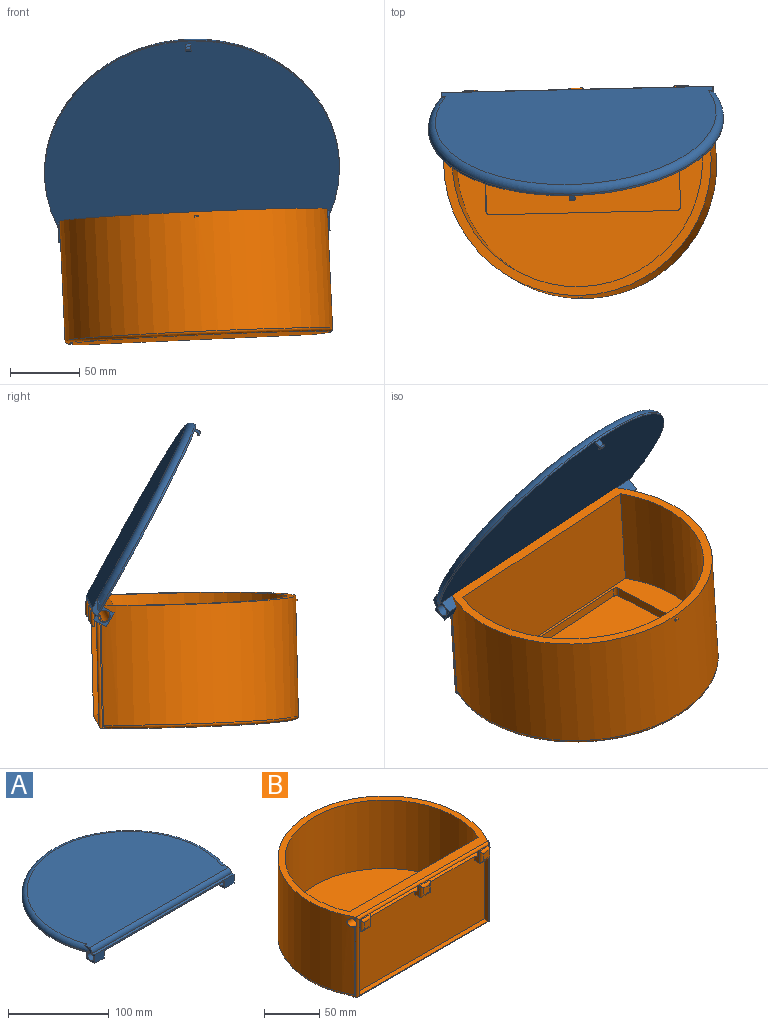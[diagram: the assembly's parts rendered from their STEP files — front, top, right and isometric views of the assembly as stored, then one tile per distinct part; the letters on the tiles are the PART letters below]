
ASSEMBLY  parts=2 mates=1
PART A: 29 faces, bbox 230.7x165x15.4 mm
  f0: plane 169.48x3.67mm, normal (0,0,-1), area 621.6mm2, adj f19,f20,f24,f27
  f1: plane 213.09x148.55mm, normal (0,0,-1), area 26333.1mm2, adj f2,f3,f4,f5,f11,f12,f15,f19
  f2: plane 15.37x14.01mm, normal (-1,0,0), area 79.2mm2, adj f1,f3,f6,f7,f8,f10,f21,f23
  f3: cylinder r=106.54mm len=213.09mm, axis (0,0,-1), area 534.7mm2, adj f1,f2,f5,f7,f27,f28
  f4: plane 5.72x3.64mm, normal (1,0,0), area 12.3mm2, adj f1,f12,f13,f14,f15,f16,f17,f18
  f5: plane 15.37x14.01mm, normal (1,0,0), area 79.2mm2, adj f1,f3,f6,f7,f8,f9,f21,f22
  f6: cylinder r=5.08mm len=195.82mm, axis (1,0,0), area 1318.5mm2, adj f2,f5,f8,f21
  f7: torus R=101.46mm, axis (0,0,1), area 3251.5mm2, adj f2,f3,f5,f8,f9,f10
  f8: plane 202.93x143.47mm, normal (0,0,1), area 24499mm2, adj f2,f5,f6,f7,f9,f10
  f9: plane 2.98x0.86mm, normal (0,1,0), area 0.8mm2, adj f5,f7,f8
  f10: plane 2.98x0.86mm, normal (0,1,0), area 0.8mm2, adj f2,f7,f8
  f11: plane 5.72x3.64mm, normal (-1,0,0), area 12.3mm2, adj f1,f12,f13,f14,f15,f16,f17,f18
  f12: plane 4.45x3.81mm, normal (0,1,0), area 16.9mm2, adj f1,f4,f11,f18
  f13: plane 3.81x1.27mm, normal (0,0,-1), area 4.8mm2, adj f4,f11,f16,f18
  f14: plane 3.81x0.64mm, normal (0,0,1), area 2.4mm2, adj f4,f11,f15,f17
  f15: plane 4.45x3.81mm, normal (0,-1,0), area 16.9mm2, adj f1,f4,f11,f14
  f16: cylinder r=1.27mm len=3.81mm, axis (1,0,0), area 5.1mm2, adj f4,f11,f13,f17
  f17: cylinder r=1.27mm len=3.81mm, axis (-1,0,0), area 5.1mm2, adj f4,f11,f14,f16
  f18: cylinder r=1.27mm len=3.81mm, axis (-1,0,0), area 7.6mm2, adj f4,f11,f12,f13
  f19: plane 11.47x9.02mm, normal (-1,0,0), area 43.3mm2, adj f0,f1,f22,f24,f25,f27
  f20: plane 11.47x9.02mm, normal (1,0,0), area 43.3mm2, adj f0,f1,f23,f24,f26,f27
  f21: plane 195.82x3.81mm, normal (0,0,1), area 746.1mm2, adj f2,f5,f6,f24
  f22: plane 13.17x9.02mm, normal (0,1,0), area 118.7mm2, adj f1,f5,f19,f25
  f23: plane 13.17x9.02mm, normal (0,1,0), area 118.7mm2, adj f1,f2,f20,f26
  f24: plane 195.82x10.44mm, normal (0,-1,0), area 516mm2, adj f0,f2,f5,f19,f20,f21,f25,f26
  f25: plane 13.17x11.47mm, normal (0,0,-1), area 151mm2, adj f5,f19,f22,f24
  f26: plane 13.17x11.47mm, normal (0,0,-1), area 151mm2, adj f2,f20,f23,f24
  f27: cylinder r=4.45mm len=196.08mm, axis (-1,0,0), area 1555.7mm2, adj f0,f1,f2,f3,f5,f19,f20,f28
  f28: plane 0.61x0.31mm, normal (1,0,0), area 0.1mm2, adj f1,f3,f27
PART B: 69 faces, bbox 209.2x157.8x88.9 mm
  f0: plane 71.12x5.08mm, normal (-1,0,0), area 361.3mm2, adj f3,f23,f36,f47
  f1: plane 71.12x5.08mm, normal (1,0,0), area 361.3mm2, adj f3,f20,f36,f46
  f2: cylinder r=96.65mm len=193.3mm, axis (0,0,-1), area 34407mm2, adj f13,f14,f15,f16,f18,f24,f30,f31
  f3: plane 164.83x74.94mm, normal (0,-1,0), area 12206.7mm2, adj f0,f1,f5,f6,f8,f10,f30,f36
  f4: plane 1.02x0.12mm, normal (1,0,0), area 0mm2, adj f7,f30,f39
  f5: plane 12.7x6.6mm, normal (1,0,0), area 51.9mm2, adj f3,f30,f39,f48,f55,f68
  f6: plane 12.7x6.6mm, normal (-1,0,0), area 51.9mm2, adj f3,f30,f39,f47,f53,f61
  f7: plane 63.37x0.12mm, normal (0,-1,0), area 7.5mm2, adj f4,f30,f38,f39
  f8: plane 12.7x6.6mm, normal (1,0,0), area 51.9mm2, adj f3,f30,f41,f46,f50,f59
  f9: plane 1.02x0.12mm, normal (-1,0,0), area 0mm2, adj f11,f30,f41
  f10: plane 12.7x6.6mm, normal (-1,0,0), area 51.9mm2, adj f3,f30,f41,f48,f55,f65
  f11: plane 63.37x0.12mm, normal (0,-1,0), area 7.5mm2, adj f9,f30,f40,f41
  f12: plane 180.6x127.25mm, normal (0,0,1), area 9485mm2, adj f17,f25,f26,f27,f28,f37,f42,f43
  f13: plane 78.46x6.38mm, normal (1,0,0), area 64.1mm2, adj f2,f19,f23,f24,f30
  f14: plane 78.46x6.38mm, normal (-1,0,0), area 64.1mm2, adj f2,f19,f20,f24,f30
  f15: plane 3.53x0.78mm, normal (-1,0,0), area 2.5mm2, adj f2,f18,f20,f30
  f16: plane 3.53x0.78mm, normal (1,0,0), area 2.5mm2, adj f2,f18,f23,f30
  f17: cylinder r=90.3mm len=180.6mm, axis (0,0,-1), area 27236.1mm2, adj f12,f18,f37
  f18: plane 193.3x143.51mm, normal (0,0,1), area 4071.9mm2, adj f2,f15,f16,f17,f21,f37
  f19: plane 188.22x140.97mm, normal (0,0,-1), area 22373mm2, adj f13,f14,f22,f24
  f20: cylinder r=2.54mm len=88.9mm, axis (0,0,-1), area 338.9mm2, adj f1,f14,f15,f21,f22,f30,f49
  f21: cylinder r=2.54mm len=169.91mm, axis (-1,0,0), area 670.6mm2, adj f18,f20,f23,f39,f41,f50,f53,f55
  f22: cylinder r=2.54mm len=169.91mm, axis (1,0,0), area 670.6mm2, adj f19,f20,f23,f36
  f23: cylinder r=2.54mm len=88.9mm, axis (0,0,-1), area 338.9mm2, adj f0,f13,f16,f21,f22,f30,f52
  f24: torus R=94.11mm, axis (0,0,1), area 1565.5mm2, adj f2,f13,f14,f19
  f25: plane 64.77x6.86mm, normal (1,0,0), area 444.2mm2, adj f12,f29,f42,f45
  f26: plane 135.38x6.86mm, normal (0,1,0), area 928.4mm2, adj f12,f29,f42,f43
  f27: plane 64.77x6.86mm, normal (-1,0,0), area 444.2mm2, adj f12,f29,f43,f44
  f28: plane 135.38x6.86mm, normal (0,-1,0), area 928.4mm2, adj f12,f29,f44,f45
  f29: plane 140.46x69.85mm, normal (0,0,1), area 9805.7mm2, adj f25,f26,f27,f28,f42,f43,f44,f45
  f30: cylinder r=4.45mm len=176.31mm, axis (-1,0,0), area 2945.6mm2, adj f2,f3,f4,f5,f6,f7,f8,f9
  f31: plane 2.54x1.28mm, normal (0,0,1), area 3.2mm2, adj f2,f32,f34,f35
  f32: plane 1.28x1.02mm, normal (-1,0,0), area 1.3mm2, adj f2,f31,f33,f35
  f33: plane 2.54x1.28mm, normal (0,0,-1), area 3.2mm2, adj f2,f32,f34,f35
  f34: plane 1.28x1.02mm, normal (1,0,0), area 1.3mm2, adj f2,f31,f33,f35
  f35: plane 2.54x1.02mm, normal (0,1,0), area 2.6mm2, adj f31,f32,f33,f34
  f36: plane 164.83x5.08mm, normal (0,0,1), area 837.4mm2, adj f0,f1,f3,f22
  f37: plane 164.78x75.69mm, normal (0,1,0), area 12472.5mm2, adj f12,f17,f18
  f38: plane 1.02x0.12mm, normal (-1,0,0), area 0mm2, adj f7,f30,f39
  f39: plane 63.37x6.35mm, normal (0,0,-1), area 402.4mm2, adj f4,f5,f6,f7,f21,f38
  f40: plane 1.02x0.12mm, normal (1,0,0), area 0mm2, adj f11,f30,f41
  f41: plane 63.37x6.35mm, normal (0,0,-1), area 402.4mm2, adj f8,f9,f10,f11,f21,f40
  f42: cylinder r=2.54mm len=6.86mm, axis (0,0,-1), area 27.4mm2, adj f12,f25,f26,f29
  f43: cylinder r=2.54mm len=6.86mm, axis (0,0,1), area 27.4mm2, adj f12,f26,f27,f29
  f44: cylinder r=2.54mm len=6.86mm, axis (0,0,-1), area 27.4mm2, adj f12,f27,f28,f29
  f45: cylinder r=2.54mm len=6.86mm, axis (0,0,1), area 27.4mm2, adj f12,f25,f28,f29
  f46: plane 12.7x6.35mm, normal (0,0,-1), area 80.6mm2, adj f1,f3,f8,f49,f60
  f47: plane 12.7x6.35mm, normal (0,0,-1), area 80.6mm2, adj f0,f3,f6,f52,f62
  f48: plane 12.7x6.35mm, normal (0,0,-1), area 80.6mm2, adj f3,f5,f10,f67
  f49: plane 12.7x1.27mm, normal (-1,0,0), area 16.1mm2, adj f20,f46,f50,f58
  f50: plane 12.7x1.27mm, normal (0,0,1), area 16.1mm2, adj f8,f21,f49,f57
  f51: plane 7.62x7.62mm, normal (0,-1,0), area 58.1mm2, adj f57,f58,f59,f60
  f52: plane 12.7x1.27mm, normal (1,0,0), area 16.1mm2, adj f23,f47,f53,f64
  f53: plane 12.7x1.27mm, normal (0,0,1), area 16.1mm2, adj f6,f21,f52,f63
  f54: plane 7.62x7.62mm, normal (0,-1,0), area 58.1mm2, adj f61,f62,f63,f64
  f55: plane 12.7x1.27mm, normal (0,0,1), area 16.1mm2, adj f5,f10,f21,f66
  f56: plane 7.62x7.62mm, normal (0,-1,0), area 58.1mm2, adj f65,f66,f67,f68
  f57: cylinder r=2.54mm len=12.7mm, axis (1,0,0), area 43.3mm2, adj f50,f51,f58,f59
  f58: cylinder r=2.54mm len=12.7mm, axis (0,0,-1), area 43.3mm2, adj f49,f51,f57,f60
  f59: cylinder r=2.54mm len=12.7mm, axis (0,0,-1), area 43.3mm2, adj f8,f51,f57,f60
  f60: cylinder r=2.54mm len=12.7mm, axis (-1,0,0), area 43.3mm2, adj f46,f51,f58,f59
  f61: cylinder r=2.54mm len=12.7mm, axis (0,0,1), area 43.3mm2, adj f6,f54,f62,f63
  f62: cylinder r=2.54mm len=12.7mm, axis (-1,0,0), area 43.3mm2, adj f47,f54,f61,f64
  f63: cylinder r=2.54mm len=12.7mm, axis (1,0,0), area 43.3mm2, adj f53,f54,f61,f64
  f64: cylinder r=2.54mm len=12.7mm, axis (0,0,-1), area 43.3mm2, adj f52,f54,f62,f63
  f65: cylinder r=2.54mm len=12.7mm, axis (0,0,1), area 43.3mm2, adj f10,f56,f66,f67
  f66: cylinder r=2.54mm len=12.7mm, axis (1,0,0), area 43.3mm2, adj f55,f56,f65,f68
  f67: cylinder r=2.54mm len=12.7mm, axis (-1,0,0), area 43.3mm2, adj f48,f56,f65,f68
  f68: cylinder r=2.54mm len=12.7mm, axis (0,0,-1), area 43.3mm2, adj f5,f56,f66,f67
PLACE A rot(axis=(-0.03,0.51,0.86),179.8deg) t=(71.63,57.13,-162.83)mm
PLACE B rot(axis=(0.02,-0.01,-1),178.7deg) t=(74.58,52.82,-250.16)mm
MATE revolute A.f27 <-> B.f30  axis (-1,-0.02,-0.04) through (-25.87,53.52,-172.71)mm
